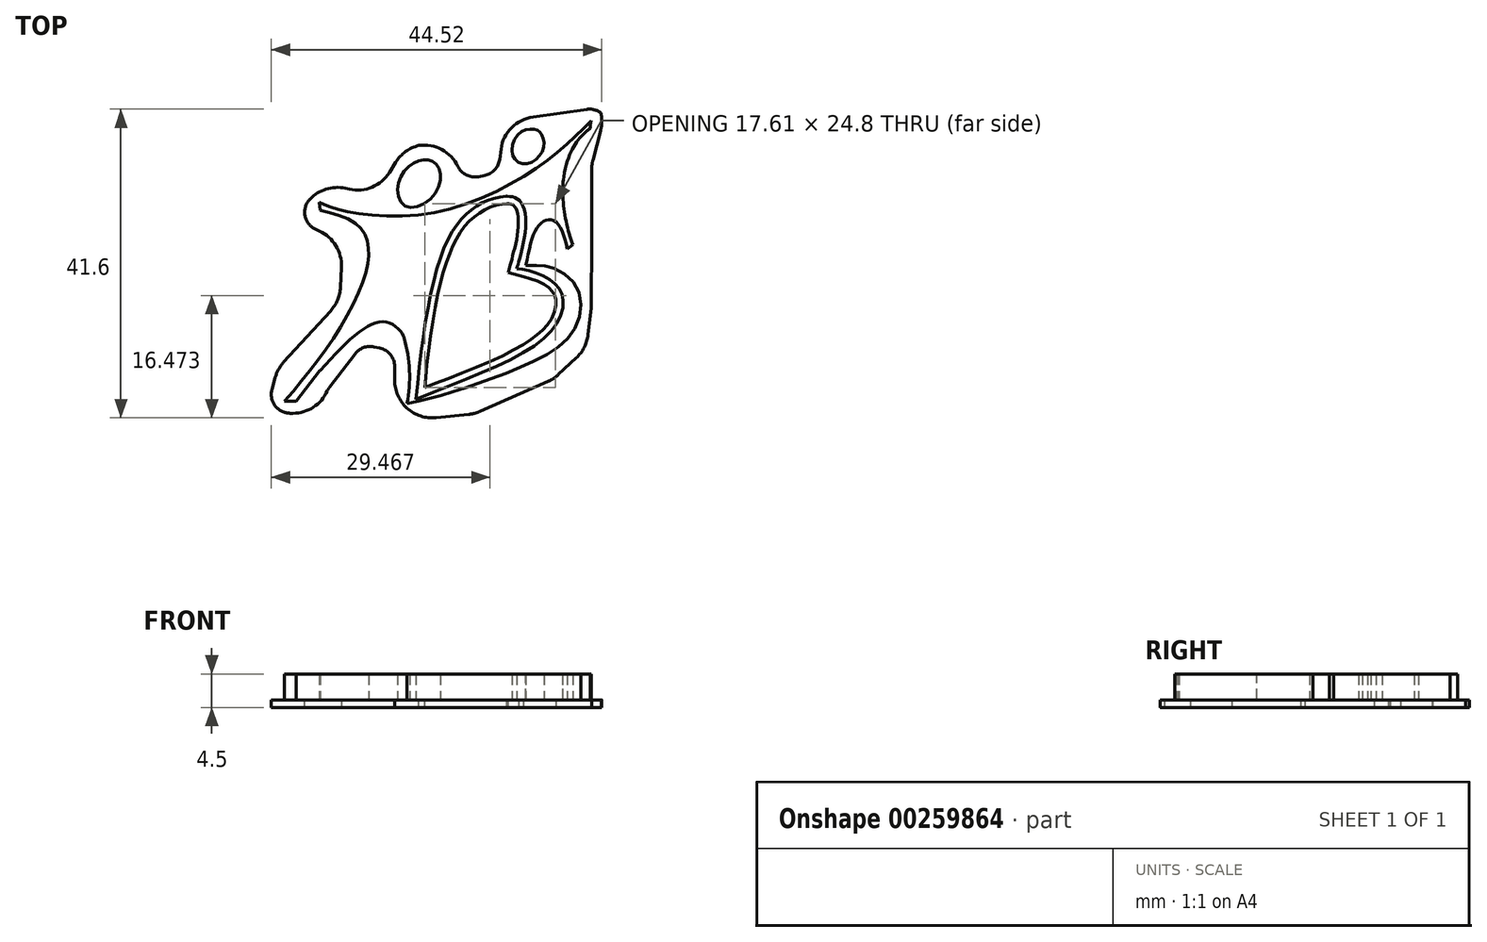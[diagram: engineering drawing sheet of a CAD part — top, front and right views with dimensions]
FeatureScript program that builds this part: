
annotation { "Feature Type Name" : "Feature", "Feature Type Description" : "" }
export const myFeature = defineFeature(function(context is Context, id is Id, definition is map)
    precondition{}
    {
        {
            var Q0;
            Q0=qCreatedBy(makeId("Top.planeOp"),FACE);
            var sketch = newSketch(context, id + "F0", { "sketchPlane" : qUnion([Q0])});
            skSolve(sketch);
        }
        {
            var Q0;
            Q0=qCreatedBy(makeId("Top.planeOp"),FACE);
            var sketch = newSketch(context, id + "F1", { "sketchPlane" : qUnion([Q0])});
            skLineSegment(sketch, "E0", {"start": v(-22.23, -15.3) * mm, "end": v(-20.65, -15.3) * mm});
            skLineSegment(sketch, "E1", {"start": v(-20.65, -15.3) * mm, "end": v(-17.45, -11.2) * mm});
            skFitSpline(sketch, "E2", {"points": [v(-17.45, -11.2) * mm, v(-8.51, -4.63) * mm, v(-6.14, -6.75) * mm, v(-7.07, -6.8) * mm], "startDerivative": vector(19.75, 21.9) * mm, "endDerivative": vector(-15.69, 8.33) * mm});
            skArc(sketch, "E3", {"start": v(-5.72, -15.63) * mm, "mid": v(-5.4, -11.17) * mm, "end": v(-6.14, -6.75) * mm});
            skFitSpline(sketch, "E4", {"points": [v(-5.72, -15.63) * mm, v(-0.92, -14.47) * mm, v(5.1, -12.44) * mm, v(12.73, -9.22) * mm, v(17.05, -5.18) * mm, v(17.17, 0) * mm, v(13.47, 2.8) * mm, v(10.3, 3) * mm], "startDerivative": vector(34.78, 7.68) * mm, "endDerivative": vector(-38.22, 1.94) * mm});
            skFitSpline(sketch, "E5", {"points": [v(10.3, 3) * mm, v(11.39, 7.3) * mm, v(12.53, 8.85) * mm, v(13.69, 9.14) * mm, v(14.78, 8.36) * mm, v(15.86, 5.23) * mm], "startDerivative": vector(3.36, 17.25) * mm, "endDerivative": vector(3.7, -15.07) * mm});
            skLineSegment(sketch, "E6", {"start": v(15.86, 5.23) * mm, "end": v(16.6, 5.76) * mm});
            skFitSpline(sketch, "E7", {"points": [v(16.6, 5.76) * mm, v(15.38, 14.9) * mm], "startDerivative": vector(-2.98, 8.18) * mm, "endDerivative": vector(1.32, 7.42) * mm});
            skFitSpline(sketch, "E8", {"points": [v(15.38, 14.9) * mm, v(18.94, 21.45) * mm], "startDerivative": vector(1.84, 13.75) * mm, "endDerivative": vector(1.32, 1.18) * mm});
            skArc(sketch, "E9", {"start": v(19.1, 22.47) * mm, "mid": v(18.97, 21.97) * mm, "end": v(18.94, 21.45) * mm});
            skFitSpline(sketch, "E10", {"points": [v(19.1, 22.47) * mm, v(12.12, 16.4) * mm, v(-2.4, 10.06) * mm, v(-14.73, 10.44) * mm, v(-17.58, 11.48) * mm], "startDerivative": vector(-23.65, -23.54) * mm, "endDerivative": vector(-15.68, 7.56) * mm});
            skLineSegment(sketch, "E11", {"start": v(-17.58, 11.48) * mm, "end": v(-17.43, 10.39) * mm});
            skFitSpline(sketch, "E12", {"points": [v(-17.43, 10.39) * mm, v(-12.47, 8.5) * mm, v(-11, 5.86) * mm, v(-11.35, 1.72) * mm, v(-15.54, -6.69) * mm, v(-22.23, -15.3) * mm], "startDerivative": vector(29.21, -6.18) * mm, "endDerivative": vector(-26.72, -31.44) * mm});
            skFitSpline(sketch, "E13", {"points": [v(-2.86, 17.2) * mm, v(-5.12, 16.63) * mm, v(-6.97, 13.58) * mm, v(-5.75, 10.9) * mm, v(-1.99, 12.57) * mm, v(-1.47, 16.11) * mm, v(-2.86, 17.2) * mm]});
            skFitSpline(sketch, "E14", {"points": [v(11.4, 21.33) * mm, v(9.51, 20.88) * mm, v(8.4, 18.4) * mm, v(9.53, 16.75) * mm, v(11.7, 17.3) * mm, v(12.72, 19.32) * mm, v(12.28, 20.84) * mm, v(11.4, 21.33) * mm]});
            skFitSpline(sketch, "E15", {"points": [v(7.7, 12.33) * mm, v(3.55, 10.92) * mm, v(-0.48, 5.92) * mm, v(-4.5, -15.03) * mm], "startDerivative": vector(-21.48, -2.27) * mm, "endDerivative": vector(-4.46, -50.03) * mm});
            skFitSpline(sketch, "E16", {"points": [v(-4.5, -15.03) * mm, v(13.37, -6.23) * mm, v(15.2, -1.16) * mm, v(12.95, 1.42) * mm, v(9.07, 2.56) * mm], "startDerivative": vector(52.64, 21.5) * mm, "endDerivative": vector(-13.98, 0.35) * mm});
            skFitSpline(sketch, "E17", {"points": [v(7.7, 12.33) * mm, v(9.23, 11.89) * mm, v(10.27, 9.07) * mm, v(9.48, 4.05) * mm, v(9.07, 2.56) * mm], "startDerivative": vector(8.36, -0.77) * mm, "endDerivative": vector(-1.72, -6.4) * mm});
            skSolve(sketch);
        }
        {
            var Q0;
            Q0=qSketchRegion(id+"F1",true);
            extrude(context, id + "F2", {"entities" : qUnion([Q0]), "depth" : 3.5 * mm});
        }
        {
            var Q0;
            Q0=makeQuery(id+"F2.opExtrude","SWEPT_EDGE",EDGE,{"disambiguationData":[OSD([sQuery(id+"F1.wireOp",EDGE,"E2"),sQuery(id+"F1.wireOp",EDGE,"E3")])]});
            var Q1;
            Q1=makeQuery(id+"F2.opExtrude","SWEPT_EDGE",EDGE,{"disambiguationData":[OSD([sQuery(id+"F1.wireOp",EDGE,"E1"),sQuery(id+"F1.wireOp",EDGE,"E2")])]});
            var Q2;
            Q2=makeQuery(id+"F2.opExtrude","SWEPT_EDGE",EDGE,{"disambiguationData":[OSD([sQuery(id+"F1.wireOp",EDGE,"E7"),sQuery(id+"F1.wireOp",EDGE,"E8")])]});
            var Q3;
            Q3=makeQuery(id+"F2.opExtrude","SWEPT_EDGE",EDGE,{"disambiguationData":[OSD([sQuery(id+"F1.wireOp",EDGE,"E15"),sQuery(id+"F1.wireOp",EDGE,"E17")])]});
            fillet(context, id + "F3", {"entities" : qUnion([Q0, Q1, Q2, Q3]), "radius" : .5 * mm, "tangentPropagation" : true, "allowEdgeOverflow" : false});
        }
        {
            var Q0;
            Q0=makeQuery(id+"F2.opExtrude","CAP_FACE",FACE,{"disambiguationData":[OSD([sQuery(id+"F1.wireOp",EDGE,"E0"),sQuery(id+"F1.wireOp",EDGE,"E1"),sQuery(id+"F1.wireOp",EDGE,"E2"),sQuery(id+"F1.wireOp",EDGE,"E3"),sQuery(id+"F1.wireOp",EDGE,"E4"),sQuery(id+"F1.wireOp",EDGE,"E5"),sQuery(id+"F1.wireOp",EDGE,"E6"),sQuery(id+"F1.wireOp",EDGE,"E7"),sQuery(id+"F1.wireOp",EDGE,"E8"),sQuery(id+"F1.wireOp",EDGE,"E9"),sQuery(id+"F1.wireOp",EDGE,"E10"),sQuery(id+"F1.wireOp",EDGE,"E11"),sQuery(id+"F1.wireOp",EDGE,"E12"),sQuery(id+"F1.wireOp",EDGE,"E15"),sQuery(id+"F1.wireOp",EDGE,"E16"),sQuery(id+"F1.wireOp",EDGE,"E17")])],"isStart":true});
            var sketch = newSketch(context, id + "F4", { "sketchPlane" : qUnion([Q0])});
            skLineSegment(sketch, "E18", {"start": v(20.64, -22.35) * mm, "end": v(19.15, -16.56) * mm});
            skLineSegment(sketch, "E19", {"start": v(19.15, -16.56) * mm, "end": v(19.15, -6.23) * mm});
            skLineSegment(sketch, "E20", {"start": v(19.15, -6.23) * mm, "end": v(19.1, 2.44) * mm});
            skLineSegment(sketch, "E21", {"start": v(19.1, 2.44) * mm, "end": v(18.44, 8.19) * mm});
            skLineSegment(sketch, "E22", {"start": v(18.44, 8.19) * mm, "end": v(14.03, 12.3) * mm});
            skLineSegment(sketch, "E23", {"start": v(14.03, 12.3) * mm, "end": v(3.4, 16.99) * mm});
            skLineSegment(sketch, "E24", {"start": v(3.4, 16.99) * mm, "end": v(-7.4, 18.1) * mm});
            skLineSegment(sketch, "E25", {"start": v(-7.4, 18.1) * mm, "end": v(-7.4, 8.56) * mm});
            skLineSegment(sketch, "E26", {"start": v(-7.4, 8.56) * mm, "end": v(-11.75, 7.66) * mm});
            skLineSegment(sketch, "E27", {"start": v(-11.75, 7.66) * mm, "end": v(-16.36, 13.66) * mm});
            skLineSegment(sketch, "E28", {"start": v(-16.36, 13.66) * mm, "end": v(-17.79, 16.92) * mm});
            skLineSegment(sketch, "E29", {"start": v(-17.79, 16.92) * mm, "end": v(-24.8, 16.92) * mm});
            skLineSegment(sketch, "E30", {"start": v(-24.8, 16.92) * mm, "end": v(-23.17, 10.96) * mm});
            skLineSegment(sketch, "E31", {"start": v(-23.17, 10.96) * mm, "end": v(-14.8, 1.8) * mm});
            skLineSegment(sketch, "E32", {"start": v(-14.8, 1.8) * mm, "end": v(-14.4, -6.2) * mm});
            skLineSegment(sketch, "E33", {"start": v(-14.4, -6.2) * mm, "end": v(-20.23, -8.85) * mm});
            skLineSegment(sketch, "E34", {"start": v(-20.23, -8.85) * mm, "end": v(-19.04, -14.45) * mm});
            skLineSegment(sketch, "E35", {"start": v(-19.04, -14.45) * mm, "end": v(-10, -12.5) * mm});
            skLineSegment(sketch, "E36", {"start": v(-10, -12.5) * mm, "end": v(-6.06, -18.8) * mm});
            skLineSegment(sketch, "E37", {"start": v(-6.06, -18.8) * mm, "end": v(0, -19.93) * mm});
            skLineSegment(sketch, "E38", {"start": v(0, -19.93) * mm, "end": v(1.75, -14.54) * mm});
            skLineSegment(sketch, "E39", {"start": v(1.75, -14.54) * mm, "end": v(6.51, -15.46) * mm});
            skLineSegment(sketch, "E40", {"start": v(6.51, -15.46) * mm, "end": v(7.43, -22.47) * mm});
            skLineSegment(sketch, "E41", {"start": v(7.43, -22.47) * mm, "end": v(20.22, -24.27) * mm});
            skLineSegment(sketch, "E42", {"start": v(20.22, -24.27) * mm, "end": v(20.64, -22.35) * mm});
            skSolve(sketch);
        }
        {
            var Q0;
            Q0 = qSketchRegion(id + "F4", true);
            extrude(context, id + "F5", {"entities" : qUnion([Q0]), "operationType" : NewBodyOperationType.ADD, "depth" : 1 * mm});
        }
        {
            var Q0;
            Q0=makeQuery(id+"F5.opExtrude","SWEPT_EDGE",EDGE,{"disambiguationData":[OSD([sQuery(id+"F4.wireOp",EDGE,"E24"),sQuery(id+"F4.wireOp",EDGE,"E25")])]});
            var Q1;
            Q1=makeQuery(id+"F5.opExtrude","SWEPT_EDGE",EDGE,{"disambiguationData":[OSD([sQuery(id+"F4.wireOp",EDGE,"E23"),sQuery(id+"F4.wireOp",EDGE,"E24")])]});
            var Q2;
            Q2=makeQuery(id+"F5.opExtrude","SWEPT_EDGE",EDGE,{"disambiguationData":[OSD([sQuery(id+"F4.wireOp",EDGE,"E21"),sQuery(id+"F4.wireOp",EDGE,"E22")])]});
            var Q3;
            Q3=makeQuery(id+"F5.opExtrude","SWEPT_EDGE",EDGE,{"disambiguationData":[OSD([sQuery(id+"F4.wireOp",EDGE,"E22"),sQuery(id+"F4.wireOp",EDGE,"E23")])]});
            var Q4;
            Q4=makeQuery(id+"F5.opExtrude","SWEPT_EDGE",EDGE,{"disambiguationData":[OSD([sQuery(id+"F4.wireOp",EDGE,"E20"),sQuery(id+"F4.wireOp",EDGE,"E21")])]});
            var Q5;
            Q5=makeQuery(id+"F5.opExtrude","SWEPT_EDGE",EDGE,{"disambiguationData":[OSD([sQuery(id+"F4.wireOp",EDGE,"E18"),sQuery(id+"F4.wireOp",EDGE,"E42")])]});
            var Q6;
            Q6=makeQuery(id+"F5.opExtrude","SWEPT_EDGE",EDGE,{"disambiguationData":[OSD([sQuery(id+"F4.wireOp",EDGE,"E18"),sQuery(id+"F4.wireOp",EDGE,"E19")])]});
            var Q7;
            Q7=makeQuery(id+"F5.opExtrude","SWEPT_EDGE",EDGE,{"disambiguationData":[OSD([sQuery(id+"F4.wireOp",EDGE,"E40"),sQuery(id+"F4.wireOp",EDGE,"E41")])]});
            var Q8;
            Q8=makeQuery(id+"F5.opExtrude","SWEPT_EDGE",EDGE,{"disambiguationData":[OSD([sQuery(id+"F4.wireOp",EDGE,"E37"),sQuery(id+"F4.wireOp",EDGE,"E38")])]});
            var Q9;
            Q9=makeQuery(id+"F5.opExtrude","SWEPT_EDGE",EDGE,{"disambiguationData":[OSD([sQuery(id+"F4.wireOp",EDGE,"E36"),sQuery(id+"F4.wireOp",EDGE,"E37")])]});
            var Q10;
            Q10=makeQuery(id+"F5.opExtrude","SWEPT_EDGE",EDGE,{"disambiguationData":[OSD([sQuery(id+"F4.wireOp",EDGE,"E35"),sQuery(id+"F4.wireOp",EDGE,"E36")])]});
            var Q11;
            Q11=makeQuery(id+"F5.opExtrude","SWEPT_EDGE",EDGE,{"disambiguationData":[OSD([sQuery(id+"F4.wireOp",EDGE,"E34"),sQuery(id+"F4.wireOp",EDGE,"E35")])]});
            var Q12;
            Q12=makeQuery(id+"F5.opExtrude","SWEPT_EDGE",EDGE,{"disambiguationData":[OSD([sQuery(id+"F4.wireOp",EDGE,"E32"),sQuery(id+"F4.wireOp",EDGE,"E33")])]});
            var Q13;
            Q13=makeQuery(id+"F5.opExtrude","SWEPT_EDGE",EDGE,{"disambiguationData":[OSD([sQuery(id+"F4.wireOp",EDGE,"E31"),sQuery(id+"F4.wireOp",EDGE,"E32")])]});
            var Q14;
            Q14=makeQuery(id+"F5.opExtrude","SWEPT_EDGE",EDGE,{"disambiguationData":[OSD([sQuery(id+"F4.wireOp",EDGE,"E30"),sQuery(id+"F4.wireOp",EDGE,"E31")])]});
            var Q15;
            Q15=makeQuery(id+"F5.opExtrude","SWEPT_EDGE",EDGE,{"disambiguationData":[OSD([sQuery(id+"F4.wireOp",EDGE,"E28"),sQuery(id+"F4.wireOp",EDGE,"E29")])]});
            fillet(context, id + "F6", {"entities" : qUnion([Q0, Q1, Q2, Q3, Q4, Q5, Q6, Q7, Q8, Q9, Q10, Q11, Q12, Q13, Q14, Q15]), "radius" : 5.08 * mm, "tangentPropagation" : true, "allowEdgeOverflow" : false});
        }
        {
            var Q0;
            Q0=makeQuery(id+"F5.opExtrude","SWEPT_EDGE",EDGE,{"disambiguationData":[OSD([sQuery(id+"F4.wireOp",EDGE,"E33"),sQuery(id+"F4.wireOp",EDGE,"E34")])]});
            var Q1;
            Q1=makeQuery(id+"F5.opExtrude","SWEPT_EDGE",EDGE,{"disambiguationData":[OSD([sQuery(id+"F4.wireOp",EDGE,"E29"),sQuery(id+"F4.wireOp",EDGE,"E30")])]});
            var Q2;
            Q2=makeQuery(id+"F5.opExtrude","SWEPT_EDGE",EDGE,{"disambiguationData":[OSD([sQuery(id+"F4.wireOp",EDGE,"E27"),sQuery(id+"F4.wireOp",EDGE,"E28")])]});
            var Q3;
            Q3=makeQuery(id+"F5.opExtrude","SWEPT_EDGE",EDGE,{"disambiguationData":[OSD([sQuery(id+"F4.wireOp",EDGE,"E26"),sQuery(id+"F4.wireOp",EDGE,"E27")])]});
            var Q4;
            Q4=makeQuery(id+"F5.opExtrude","SWEPT_EDGE",EDGE,{"disambiguationData":[OSD([sQuery(id+"F4.wireOp",EDGE,"E25"),sQuery(id+"F4.wireOp",EDGE,"E26")])]});
            var Q5;
            Q5=makeQuery(id+"F5.opExtrude","SWEPT_EDGE",EDGE,{"disambiguationData":[OSD([sQuery(id+"F4.wireOp",EDGE,"E38"),sQuery(id+"F4.wireOp",EDGE,"E39")])]});
            var Q6;
            Q6=makeQuery(id+"F5.opExtrude","SWEPT_EDGE",EDGE,{"disambiguationData":[OSD([sQuery(id+"F4.wireOp",EDGE,"E39"),sQuery(id+"F4.wireOp",EDGE,"E40")])]});
            var Q7;
            Q7=makeQuery(id+"F5.opExtrude","SWEPT_EDGE",EDGE,{"disambiguationData":[OSD([sQuery(id+"F4.wireOp",EDGE,"E41"),sQuery(id+"F4.wireOp",EDGE,"E42")])]});
            fillet(context, id + "F7", {"entities" : qUnion([Q0, Q1, Q2, Q3, Q4, Q5, Q6, Q7]), "radius" : 2.54 * mm, "tangentPropagation" : true, "allowEdgeOverflow" : false});
        }
        {
            var Q0;
            {var subQ0=sQuery(id+"F1.wireOp",EDGE,"E16");Q0=makeQuery(id+"F4.imprint","IMPRINT",FACE,{"disambiguationData":[TD([[makeQuery(id+"F4.imprint","IMPRINT",EDGE,{"derivedFrom":makeQuery(id+"F2.opExtrude","CAP_EDGE",EDGE,{"disambiguationData":[OSD([subQ0])],"isStart":true})}),-1.0]])]});}
            var sketch = newSketch(context, id + "F8", { "sketchPlane" : qUnion([Q0])});
            skFitSpline(sketch, "E43.0", {"points": [v(-4.88, 14.1) * mm, v(-2.67, 13.2) * mm, v(1.71, 11.5) * mm, v(6.59, 9.44) * mm, v(9.77, 7.76) * mm, v(11.38, 6.68) * mm, v(12.4, 5.8) * mm, v(13.22, 4.93) * mm, v(13.93, 3.83) * mm, v(14.32, 2.58) * mm, v(14.32, 1.7) * mm, v(14.17, 1.13) * mm, v(14, 0.75) * mm, v(13.75, 0.4) * mm, v(13.3, -0.04) * mm, v(12.52, -0.56) * mm, v(11.23, -1.1) * mm, v(10.13, -1.4) * mm, v(9.41, -1.53) * mm, v(9.14, -1.55) * mm, v(9.05, -1.56) * mm]});
            skFitSpline(sketch, "E44.0", {"points": [v(7.8, -11.34) * mm, v(7.39, -11.3) * mm, v(6.62, -11.17) * mm, v(5.6, -10.87) * mm, v(4.66, -10.45) * mm, v(3.75, -9.87) * mm, v(2.86, -9.14) * mm, v(2, -8.21) * mm, v(1.19, -7.04) * mm, v(0.42, -5.58) * mm, v(-0.28, -3.78) * mm, v(-1.14, -0.97) * mm, v(-2.05, 3.2) * mm, v(-2.9, 8.94) * mm, v(-3.32, 13.04) * mm, v(-3.5, 15.12) * mm]});
            skFitSpline(sketch, "E45.0", {"points": [v(7.6, -11.33) * mm, v(7.78, -11.32) * mm, v(8.01, -11.3) * mm, v(8.26, -11.25) * mm, v(8.4, -11.21) * mm, v(8.51, -11.17) * mm, v(8.58, -11.12) * mm, v(8.63, -11.09) * mm, v(8.68, -11.03) * mm, v(8.77, -10.94) * mm, v(8.87, -10.77) * mm, v(9, -10.5) * mm, v(9.16, -10.03) * mm, v(9.25, -9.46) * mm, v(9.28, -8.94) * mm, v(9.27, -8.4) * mm, v(9.21, -7.64) * mm, v(9.07, -6.71) * mm, v(8.89, -5.8) * mm, v(8.69, -4.96) * mm, v(8.5, -4.24) * mm, v(8.35, -3.68) * mm, v(8.22, -3.22) * mm, v(8.14, -2.95) * mm, v(8.1, -2.82) * mm]});
            skLineSegment(sketch, "E46", {"start": v(10.5, -1.3) * mm, "end": v(7.89, -2) * mm});
            skLineSegment(sketch, "E47", {"start": v(8.1, -2.82) * mm, "end": v(7.89, -2) * mm});
            skSolve(sketch);
        }
        {
            var Q0;
            Q0 = qSketchRegion(id + "F8", true);
            extrude(context, id + "F9", {"entities" : qUnion([Q0]), "operationType" : NewBodyOperationType.REMOVE, "endBound" : BoundingType.THROUGH_ALL, "depth" : 25.4 * mm});
        }
    });
